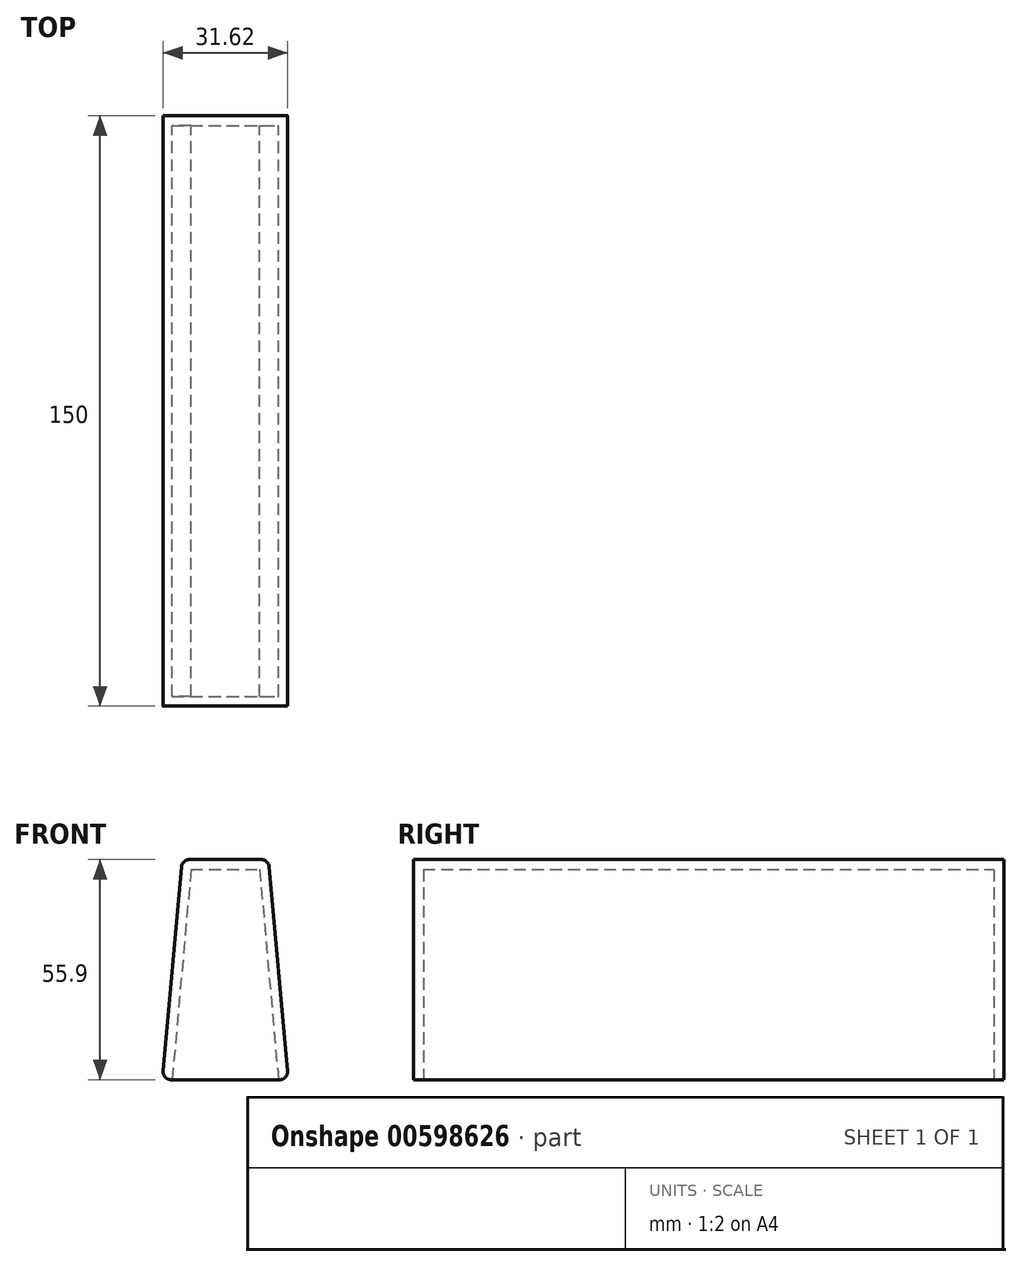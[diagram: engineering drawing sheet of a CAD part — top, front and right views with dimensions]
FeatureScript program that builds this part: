
annotation { "Feature Type Name" : "Feature", "Feature Type Description" : "" }
export const myFeature = defineFeature(function(context is Context, id is Id, definition is map)
    precondition{}
    {
        {
            var Q0;
            Q0=qCreatedBy(makeId("Front.planeOp"),FACE);
            var sketch = newSketch(context, id + "F0", { "sketchPlane" : qUnion([Q0])});
            skLineSegment(sketch, "E0", {"start": v(4.84, 54.08) * mm, "end": v(0.2, 2.18) * mm});
            skLineSegment(sketch, "E1.MirrorCS", {"start": v(27.16, 54.08) * mm, "end": v(31.8, 2.18) * mm});
            skLineSegment(sketch, "E2", {"start": v(6.83, 55.9) * mm, "end": v(25.17, 55.9) * mm});
            skLineSegment(sketch, "E3", {"start": v(2.19, 0) * mm, "end": v(29.81, 0) * mm});
            skPoint(sketch, "E4.visualSharp", {"position": v(32, 0) * mm});
            skArc(sketch, "E4.filletArc", {"start": v(29.81, 0) * mm, "mid": v(31.29, 0.65) * mm, "end": v(31.8, 2.18) * mm});
            skPoint(sketch, "E5.visualSharp", {"position": v(27, 55.9) * mm});
            skArc(sketch, "E5.filletArc", {"start": v(27.16, 54.08) * mm, "mid": v(26.52, 55.38) * mm, "end": v(25.17, 55.9) * mm});
            skPoint(sketch, "E6.visualSharp", {"position": v(5, 55.9) * mm});
            skArc(sketch, "E6.filletArc", {"start": v(6.83, 55.9) * mm, "mid": v(5.48, 55.38) * mm, "end": v(4.84, 54.08) * mm});
            skPoint(sketch, "E7.visualSharp", {"position": v(0, 0) * mm});
            skArc(sketch, "E7.filletArc", {"start": v(0.2, 2.18) * mm, "mid": v(0.71, 0.65) * mm, "end": v(2.19, 0) * mm});
            skSolve(sketch);
        }
        {
            var Q0;
            Q0=makeQuery(id+"F0.imprint","IMPRINT",FACE,{"disambiguationData":[TD([[makeQuery(id+"F0.imprint","IMPRINT",EDGE,{"derivedFrom":sQuery(id+"F0.wireOp",EDGE,"E0")}),1.0]])]});
            extrude(context, id + "F1", {"entities" : qUnion([Q0]), "depth" : 150 * mm, "offsetDistance" : 25 * mm});
        }
        {
            var Q0;
            Q0=makeQuery(id+"F1.opExtrude","SWEPT_FACE",FACE,{"disambiguationData":[OSD([sQuery(id+"F0.wireOp",EDGE,"E3")])]});
            shell(context, id + "F2", {"entities" : qUnion([Q0]), "thickness" : 2.5 * mm});
        }
    });
